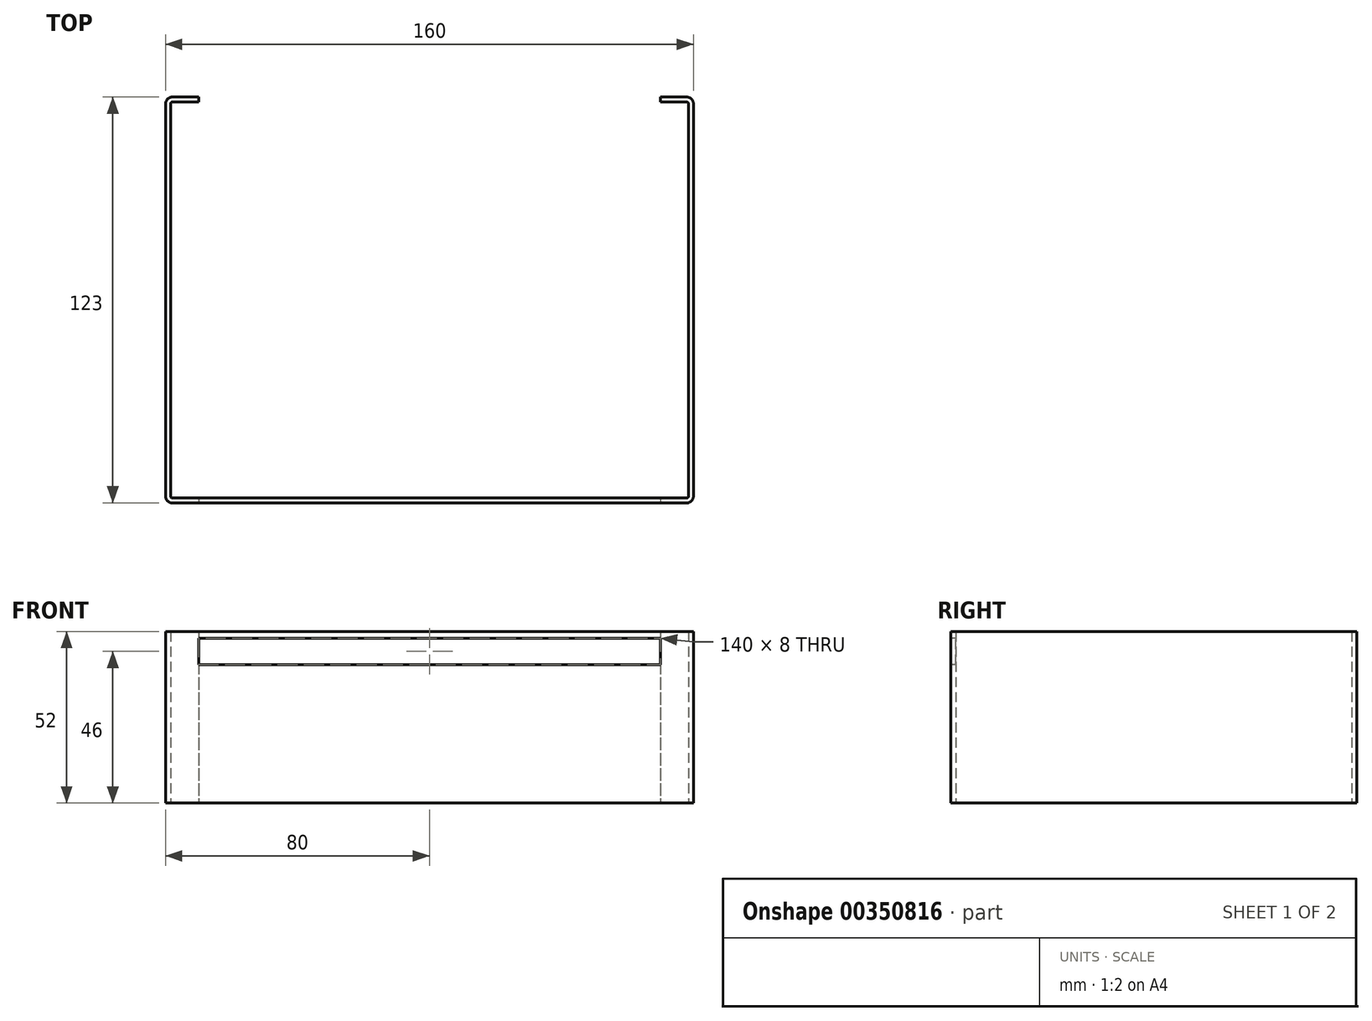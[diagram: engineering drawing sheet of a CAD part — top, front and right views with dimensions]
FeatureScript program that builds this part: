
annotation { "Feature Type Name" : "Feature", "Feature Type Description" : "" }
export const myFeature = defineFeature(function(context is Context, id is Id, definition is map)
    precondition{}
    {
        {
            var Q0;
            Q0=qCreatedBy(makeId("Top.planeOp"),FACE);
            var sketch = newSketch(context, id + "F0", { "sketchPlane" : qUnion([Q0])});
            skLineSegment(sketch, "E0", {"start": v(0, 0) * mm, "end": v(78, 0) * mm});
            skLineSegment(sketch, "E1", {"start": v(78.5, 0.5) * mm, "end": v(78.5, 119.5) * mm});
            skLineSegment(sketch, "E2", {"start": v(78, 120) * mm, "end": v(70, 120) * mm});
            skLineSegment(sketch, "E3", {"start": v(0, 13.42) * mm, "end": v(0, -8.16) * mm, "construction": true});
            skLineSegment(sketch, "E4.0", {"start": v(78, 121.5) * mm, "end": v(70, 121.5) * mm});
            skLineSegment(sketch, "E4.1", {"start": v(80, 0.5) * mm, "end": v(80, 119.5) * mm});
            skLineSegment(sketch, "E4.2", {"start": v(0, -1.5) * mm, "end": v(78, -1.5) * mm});
            skPoint(sketch, "E5.visualSharp", {"position": v(78.5, 120) * mm});
            skArc(sketch, "E5.filletArc", {"start": v(78.5, 119.5) * mm, "mid": v(78.35, 119.85) * mm, "end": v(78, 120) * mm});
            skPoint(sketch, "E6.visualSharp", {"position": v(78.5, 0) * mm});
            skArc(sketch, "E6.filletArc", {"start": v(78, 0) * mm, "mid": v(78.35, 0.15) * mm, "end": v(78.5, 0.5) * mm});
            skPoint(sketch, "E7.visualSharp", {"position": v(80, -1.5) * mm});
            skArc(sketch, "E7.filletArc", {"start": v(78, -1.5) * mm, "mid": v(79.41, -0.91) * mm, "end": v(80, 0.5) * mm});
            skPoint(sketch, "E8.visualSharp", {"position": v(80, 121.5) * mm});
            skArc(sketch, "E8.filletArc", {"start": v(80, 119.5) * mm, "mid": v(79.41, 120.91) * mm, "end": v(78, 121.5) * mm});
            skLineSegment(sketch, "E9", {"start": v(70, 121.5) * mm, "end": v(70, 120) * mm});
            skLineSegment(sketch, "E10.MirrorCS", {"start": v(-70, 121.5) * mm, "end": v(-70, 120) * mm});
            skLineSegment(sketch, "E11.MirrorCS", {"start": v(-78, 120) * mm, "end": v(-70, 120) * mm});
            skLineSegment(sketch, "E12.MirrorCS", {"start": v(-78, 121.5) * mm, "end": v(-70, 121.5) * mm});
            skLineSegment(sketch, "E13.MirrorCS", {"start": v(0, 0) * mm, "end": v(-78, 0) * mm});
            skPoint(sketch, "E14.MirrorP", {"position": v(-78.5, 120) * mm});
            skPoint(sketch, "E15.MirrorP", {"position": v(-78.5, 0) * mm});
            skPoint(sketch, "E16.MirrorP", {"position": v(-80, -1.5) * mm});
            skLineSegment(sketch, "E17.MirrorCS", {"start": v(-78.5, 0.5) * mm, "end": v(-78.5, 119.5) * mm});
            skPoint(sketch, "E18.MirrorP", {"position": v(-80, 121.5) * mm});
            skLineSegment(sketch, "E19.MirrorCS", {"start": v(-80, 0.5) * mm, "end": v(-80, 119.5) * mm});
            skLineSegment(sketch, "E20.MirrorCS", {"start": v(0, -1.5) * mm, "end": v(-78, -1.5) * mm});
            skArc(sketch, "E21.MirrorCS", {"start": v(-78, 0) * mm, "mid": v(-78.35, 0.15) * mm, "end": v(-78.5, 0.5) * mm});
            skArc(sketch, "E22.MirrorCS", {"start": v(-78, -1.5) * mm, "mid": v(-79.41, -0.91) * mm, "end": v(-80, 0.5) * mm});
            skArc(sketch, "E23.MirrorCS", {"start": v(-80, 119.5) * mm, "mid": v(-79.41, 120.91) * mm, "end": v(-78, 121.5) * mm});
            skArc(sketch, "E24.MirrorCS", {"start": v(-78.5, 119.5) * mm, "mid": v(-78.35, 119.85) * mm, "end": v(-78, 120) * mm});
            skSolve(sketch);
        }
        {
            var Q0;
            Q0 = qSketchRegion(id + "F0", true);
            extrude(context, id + "F1", {"entities" : qUnion([Q0]), "depth" : 52 * mm});
        }
        {
            var Q0;
            Q0=makeQuery(id+"F1.opExtrude","SWEPT_FACE",FACE,{"disambiguationData":[OSD([sQuery(id+"F0.wireOp",EDGE,"E4.2"),sQuery(id+"F0.wireOp",EDGE,"E20.MirrorCS")])]});
            var sketch = newSketch(context, id + "F2", { "sketchPlane" : qUnion([Q0])});
            skLineSegment(sketch, "E25.bottom", {"start": v(-70, 50) * mm, "end": v(0, 50) * mm});
            skLineSegment(sketch, "E25.top", {"start": v(-70, 42) * mm, "end": v(0, 42) * mm});
            skLineSegment(sketch, "E25.left", {"start": v(-70, 50) * mm, "end": v(-70, 42) * mm});
            skLineSegment(sketch, "E26", {"start": v(0, 0) * mm, "end": v(0, 56.24) * mm, "construction": true});
            skPoint(sketch, "E26.endSnap0", {"position": v(0, 52) * mm});
            skLineSegment(sketch, "E27.MirrorCS", {"start": v(-140, 0) * mm, "end": v(-140, 56.24) * mm, "construction": true});
            skLineSegment(sketch, "E28.MirrorCS", {"start": v(70, 50) * mm, "end": v(0, 50) * mm});
            skLineSegment(sketch, "E29.MirrorCS", {"start": v(70, 50) * mm, "end": v(70, 42) * mm});
            skLineSegment(sketch, "E30.MirrorCS", {"start": v(70, 42) * mm, "end": v(0, 42) * mm});
            skSolve(sketch);
        }
        {
            var Q0;
            Q0 = qSketchRegion(id + "F2", true);
            extrude(context, id + "F3", {"entities" : qUnion([Q0]), "operationType" : NewBodyOperationType.REMOVE, "endBound" : BoundingType.THROUGH_ALL, "oppositeDirection" : true, "depth" : 25 * mm});
        }
    });
